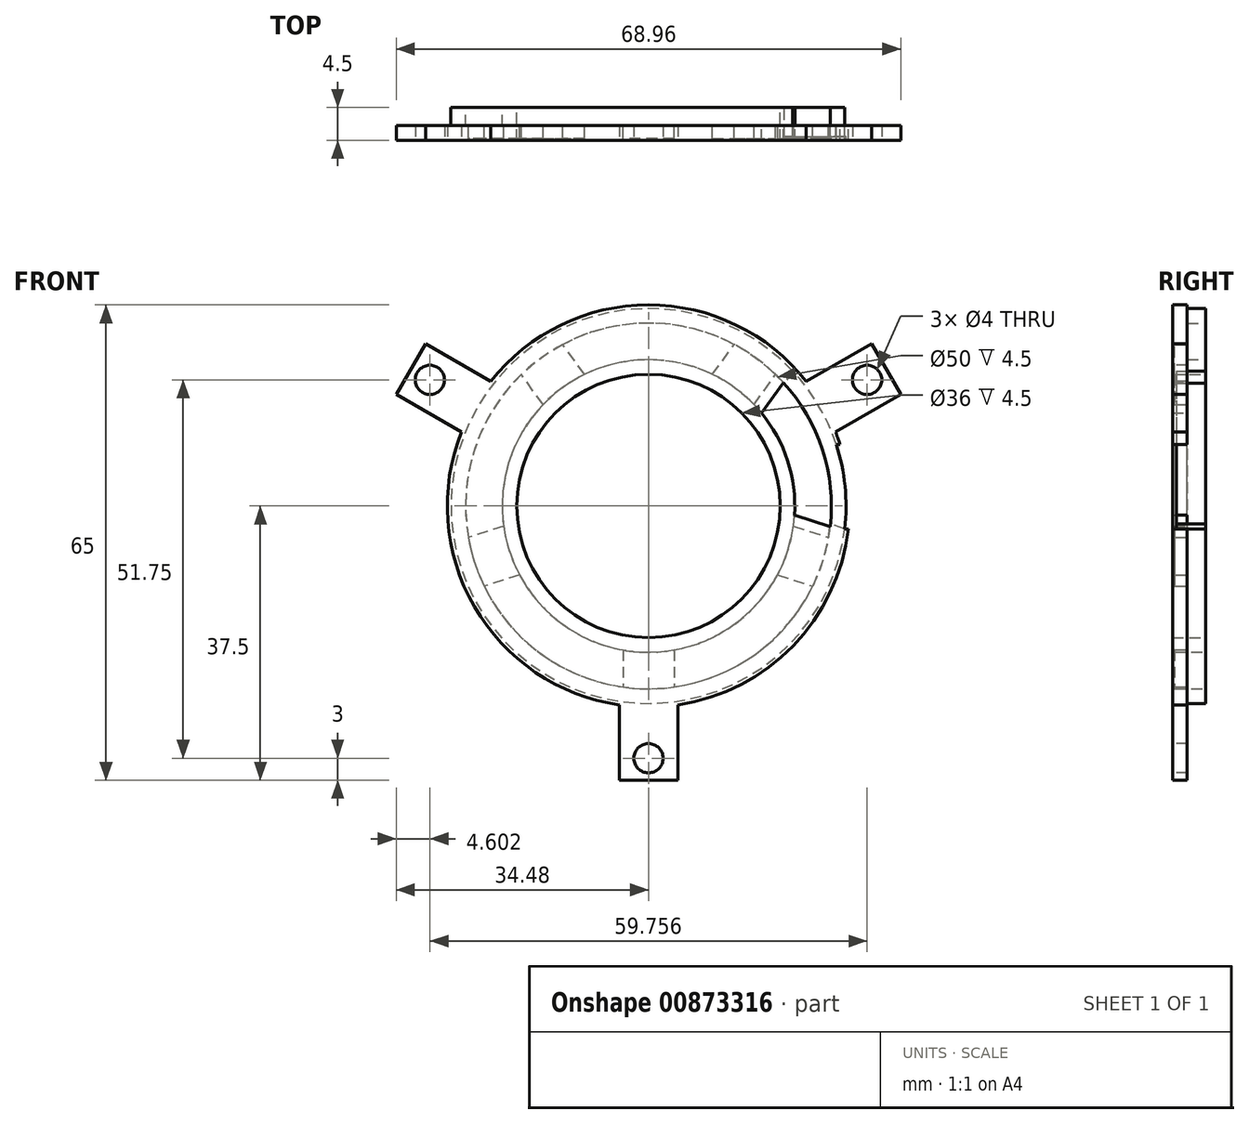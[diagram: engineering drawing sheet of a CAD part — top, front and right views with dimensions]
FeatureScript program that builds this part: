
annotation { "Feature Type Name" : "Feature", "Feature Type Description" : "" }
export const myFeature = defineFeature(function(context is Context, id is Id, definition is map)
    precondition{}
    {
        {
            var Q0;
            Q0=qCreatedBy(makeId("Right.planeOp"),FACE);
            var sketch = newSketch(context, id + "F0", { "sketchPlane" : qUnion([Q0])});
            skLineSegment(sketch, "E0", {"start": v(0, 0) * mm, "end": v(0, 18) * mm});
            skLineSegment(sketch, "E1", {"start": v(0, 18) * mm, "end": v(0, 20) * mm});
            skLineSegment(sketch, "E2", {"start": v(0, 20) * mm, "end": v(0, 25) * mm});
            skLineSegment(sketch, "E3", {"start": v(0, 25) * mm, "end": v(0, 27) * mm});
            skLineSegment(sketch, "E4", {"start": v(0, 27) * mm, "end": v(4.5, 27) * mm});
            skPoint(sketch, "E5.endSnap0", {"position": v(2.25, 27) * mm});
            skLineSegment(sketch, "E6", {"start": v(0, 22.5) * mm, "end": v(2, 22.5) * mm});
            skLineSegment(sketch, "E7", {"start": v(2, 27) * mm, "end": v(2, 0) * mm});
            skLineSegment(sketch, "E8", {"start": v(2, 0) * mm, "end": v(0, 0) * mm});
            skLineSegment(sketch, "E9", {"start": v(0, 25) * mm, "end": v(2.25, 25) * mm});
            skLineSegment(sketch, "E10", {"start": v(0, 20) * mm, "end": v(2.25, 20) * mm});
            skLineSegment(sketch, "E11", {"start": v(2, 18) * mm, "end": v(2.25, 18) * mm});
            skLineSegment(sketch, "E12", {"start": v(2, 18) * mm, "end": v(0, 18) * mm});
            skLineSegment(sketch, "E13", {"start": v(2.25, 25) * mm, "end": v(4.5, 25) * mm});
            skLineSegment(sketch, "E14", {"start": v(4.5, 25) * mm, "end": v(4.5, 27) * mm});
            skLineSegment(sketch, "E15", {"start": v(2.25, 20) * mm, "end": v(4.5, 20) * mm});
            skLineSegment(sketch, "E16", {"start": v(4.5, 20) * mm, "end": v(4.5, 18) * mm});
            skLineSegment(sketch, "E17", {"start": v(4.5, 18) * mm, "end": v(2.25, 18) * mm});
            skSolve(sketch);
        }
        {
            var Q0;
            Q0 = qSketchRegion(id + "F0", true);
            var Q1;
            Q1=sQuery(id+"F0.wireOp",EDGE,"E8");
            revolve(context, id + "F1", {"surfaceOperationType" : NewSurfaceOperationType.NEW, "entities" : qUnion([Q0]), "axis" : qUnion([Q1]), "revolveType" : RevolveType.FULL});
        }
        {
            var Q0;
            {var subQ0=sQuery(id+"F0.wireOp",EDGE,"E7");var subQ1=makeQuery(id+"F0.imprint","INTERSECT",VERTEX,{"derivedFrom":[sQuery(id+"F0.wireOp",EDGE,"E6"),subQ0]});Q0=makeQuery(id+"F1.opRevolve","SWEPT_FACE",FACE,{"disambiguationData":[OSD([subQ0]),TDD([makeQuery(id+"F0.imprint","IMPRINT",EDGE,{"disambiguationData":[TD([[subQ1,1.0]])],"derivedFrom":subQ0}),makeQuery(id+"F0.imprint","IMPRINT",EDGE,{"disambiguationData":[TD([[subQ1,-1.0]])],"derivedFrom":subQ0})])]});}
            var sketch = newSketch(context, id + "F2", { "sketchPlane" : qUnion([Q0])});
            skCircle(sketch, "E18", {"center": v(0, 0) * mm, "radius": 25 * mm});
            skCircle(sketch, "E19", {"center": v(0, 0) * mm, "radius": 20 * mm});
            skLineSegment(sketch, "E20", {"start": v(0, -20) * mm, "end": v(0, -25) * mm});
            skLineSegment(sketch, "E21", {"start": v(0, -22.5) * mm, "end": v(3.5, -22.5) * mm});
            skLineSegment(sketch, "E22", {"start": v(3.5, -19.7) * mm, "end": v(3.5, -24.75) * mm});
            skLineSegment(sketch, "E23.MirrorCS", {"start": v(-3.5, -19.7) * mm, "end": v(-3.5, -24.75) * mm});
            skLineSegment(sketch, "E24.1.0", {"start": v(19.8, -2.76) * mm, "end": v(24.62, -4.32) * mm});
            skLineSegment(sketch, "E24.1.1", {"start": v(17.65, -9.41) * mm, "end": v(22.46, -10.98) * mm});
            skLineSegment(sketch, "E24.2.0", {"start": v(8.74, 17.99) * mm, "end": v(11.72, 22.08) * mm});
            skLineSegment(sketch, "E24.2.1", {"start": v(14.4, 13.87) * mm, "end": v(17.38, 17.97) * mm});
            skLineSegment(sketch, "E24.3.0", {"start": v(-14.4, 13.87) * mm, "end": v(-17.38, 17.97) * mm});
            skLineSegment(sketch, "E24.3.1", {"start": v(-8.74, 17.99) * mm, "end": v(-11.72, 22.08) * mm});
            skLineSegment(sketch, "E24.4.0", {"start": v(-17.65, -9.41) * mm, "end": v(-22.46, -10.98) * mm});
            skLineSegment(sketch, "E24.4.1", {"start": v(-19.8, -2.76) * mm, "end": v(-24.62, -4.32) * mm});
            skLineSegment(sketch, "E25", {"start": v(-22.22, -3.54) * mm, "end": v(-22.68, -2.11) * mm});
            skLineSegment(sketch, "E26", {"start": v(-15.9, 15.92) * mm, "end": v(-17.1, 15.04) * mm});
            skCircle(sketch, "E27", {"center": v(0, 0) * mm, "radius": 27 * mm});
            skLineSegment(sketch, "E28", {"start": v(-22.68, -2.11) * mm, "end": v(-26.78, -3.44) * mm});
            skLineSegment(sketch, "E29", {"start": v(-26.78, -3.44) * mm, "end": v(-19.96, -1.23) * mm});
            skLineSegment(sketch, "E30", {"start": v(-17.1, 15.04) * mm, "end": v(-19.64, 18.53) * mm});
            skLineSegment(sketch, "E31", {"start": v(-19.64, 18.53) * mm, "end": v(-15.43, 12.73) * mm});
            skSolve(sketch);
        }
        {
            var Q0;
            {var subQ0=sQuery(id+"F2.wireOp",EDGE,"E24.4.0");Q0=makeQuery(id+"F2.imprint","IMPRINT",FACE,{"disambiguationData":[TD([[makeQuery(id+"F2.imprint","IMPRINT",EDGE,{"derivedFrom":subQ0}),-1.0]])]});}
            var Q1;
            {var subQ0=sQuery(id+"F2.wireOp",EDGE,"E24.3.0");Q1=makeQuery(id+"F2.imprint","IMPRINT",FACE,{"disambiguationData":[TD([[makeQuery(id+"F2.imprint","IMPRINT",EDGE,{"derivedFrom":subQ0}),-1.0]])]});}
            var Q2;
            {var subQ0=sQuery(id+"F2.wireOp",EDGE,"E24.2.0");Q2=makeQuery(id+"F2.imprint","IMPRINT",FACE,{"disambiguationData":[TD([[makeQuery(id+"F2.imprint","IMPRINT",EDGE,{"derivedFrom":subQ0}),-1.0]])]});}
            var Q3;
            {var subQ6=sQuery(id+"F2.wireOp",EDGE,"E23.MirrorCS");Q3=makeQuery(id+"F2.imprint","IMPRINT",FACE,{"disambiguationData":[TD([[makeQuery(id+"F2.imprint","IMPRINT",EDGE,{"derivedFrom":subQ6}),1.0]])]});}
            var Q4;
            {var subQ5=sQuery(id+"F2.wireOp",EDGE,"E21");Q4=makeQuery(id+"F2.imprint","IMPRINT",FACE,{"disambiguationData":[TD([[makeQuery(id+"F2.imprint","IMPRINT",EDGE,{"derivedFrom":subQ5}),1.0]])]});}
            var Q5;
            {var subQ5=sQuery(id+"F2.wireOp",EDGE,"E21");Q5=makeQuery(id+"F2.imprint","IMPRINT",FACE,{"disambiguationData":[TD([[makeQuery(id+"F2.imprint","IMPRINT",EDGE,{"derivedFrom":subQ5}),-1.0]])]});}
            var Q6;
            {var subQ0=sQuery(id+"F2.wireOp",EDGE,"E24.1.0");Q6=makeQuery(id+"F2.imprint","IMPRINT",FACE,{"disambiguationData":[TD([[makeQuery(id+"F2.imprint","IMPRINT",EDGE,{"derivedFrom":subQ0}),-1.0]])]});}
            extrude(context, id + "F3", {"entities" : qUnion([Q0, Q1, Q2, Q3, Q4, Q5, Q6]), "operationType" : NewBodyOperationType.REMOVE, "oppositeDirection" : true, "depth" : .6 * mm, "offsetDistance" : 25 * mm});
        }
        {
            var Q0;
            {var subQ0=sQuery(id+"F2.wireOp",EDGE,"E24.2.0");Q0=makeQuery(id+"F2.imprint","IMPRINT",FACE,{"disambiguationData":[TD([[makeQuery(id+"F2.imprint","IMPRINT",EDGE,{"derivedFrom":subQ0}),-1.0]])]});}
            var Q1;
            {var subQ0=sQuery(id+"F2.wireOp",EDGE,"E24.3.1");Q1=makeQuery(id+"F2.imprint","IMPRINT",FACE,{"disambiguationData":[TD([[makeQuery(id+"F2.imprint","IMPRINT",EDGE,{"derivedFrom":subQ0}),1.0]])]});}
            var Q2;
            {var subQ0=sQuery(id+"F2.wireOp",EDGE,"E24.1.0");Q2=makeQuery(id+"F2.imprint","IMPRINT",FACE,{"disambiguationData":[TD([[makeQuery(id+"F2.imprint","IMPRINT",EDGE,{"derivedFrom":subQ0}),-1.0]])]});}
            var Q3;
            {var subQ3=sQuery(id+"F2.wireOp",EDGE,"E23.MirrorCS");Q3=makeQuery(id+"F2.imprint","IMPRINT",FACE,{"disambiguationData":[TD([[makeQuery(id+"F2.imprint","IMPRINT",EDGE,{"derivedFrom":subQ3}),1.0]])]});}
            var Q4;
            {var subQ3=sQuery(id+"F2.wireOp",EDGE,"E21");Q4=makeQuery(id+"F2.imprint","IMPRINT",FACE,{"disambiguationData":[TD([[makeQuery(id+"F2.imprint","IMPRINT",EDGE,{"derivedFrom":subQ3}),1.0]])]});}
            var Q5;
            {var subQ3=sQuery(id+"F2.wireOp",EDGE,"E21");Q5=makeQuery(id+"F2.imprint","IMPRINT",FACE,{"disambiguationData":[TD([[makeQuery(id+"F2.imprint","IMPRINT",EDGE,{"derivedFrom":subQ3}),-1.0]])]});}
            var Q6;
            {var subQ1=sQuery(id+"F2.wireOp",EDGE,"E24.4.0");Q6=makeQuery(id+"F2.imprint","IMPRINT",FACE,{"disambiguationData":[TD([[makeQuery(id+"F2.imprint","IMPRINT",EDGE,{"derivedFrom":subQ1}),-1.0]])]});}
            extrude(context, id + "F4", {"entities" : qUnion([Q0, Q1, Q2, Q3, Q4, Q5, Q6]), "operationType" : NewBodyOperationType.REMOVE, "oppositeDirection" : true, "depth" : 1.75 * mm, "offsetDistance" : 25 * mm});
        }
        {
            var Q0;
            Q0=makeQuery(id+"F1.opRevolve","SWEPT_FACE",FACE,{"disambiguationData":[OSD([sQuery(id+"F0.wireOp",EDGE,"E14")])]});
            var sketch = newSketch(context, id + "F5", { "sketchPlane" : qUnion([Q0])});
            skCircle(sketch, "E32", {"center": v(0, 0) * mm, "radius": 27 * mm});
            skCircle(sketch, "E33", {"center": v(0, 0) * mm, "radius": 25 * mm});
            skLineSegment(sketch, "E34", {"start": v(-26.82, -3.14) * mm, "end": v(-24.88, -2.45) * mm});
            skLineSegment(sketch, "E35", {"start": v(-19.72, 18.44) * mm, "end": v(-18.55, 16.76) * mm});
            skSolve(sketch);
        }
        {
            var Q0;
            {var subQ0=sQuery(id+"F5.wireOp",EDGE,"E34");Q0=makeQuery(id+"F5.imprint","IMPRINT",FACE,{"disambiguationData":[TD([[makeQuery(id+"F5.imprint","IMPRINT",EDGE,{"derivedFrom":subQ0}),1.0]])]});}
            extrude(context, id + "F6", {"entities" : qUnion([Q0]), "operationType" : NewBodyOperationType.REMOVE, "oppositeDirection" : true, "depth" : 4 * mm, "offsetDistance" : 25 * mm});
        }
        {
            var Q0;
            {var subQ6=sQuery(id+"F2.wireOp",EDGE,"E29");var subQ7=makeQuery(id+"F2.imprint","INTERSECT",VERTEX,{"derivedFrom":[sQuery(id+"F2.wireOp",EDGE,"E25"),subQ6]});Q0=makeQuery(id+"F2.imprint","IMPRINT",FACE,{"disambiguationData":[TD([[makeQuery(id+"F2.imprint","IMPRINT",EDGE,{"disambiguationData":[TD([[subQ7,1.0]])],"derivedFrom":subQ6}),1.0]])]});}
            var sketch = newSketch(context, id + "F7", { "sketchPlane" : qUnion([Q0])});
            skCircle(sketch, "E36", {"center": v(0, 0) * mm, "radius": 18 * mm});
            skSolve(sketch);
        }
        {
            var Q0;
            Q0 = qSketchRegion(id + "F7", true);
            extrude(context, id + "F8", {"entities" : qUnion([Q0]), "operationType" : NewBodyOperationType.REMOVE, "oppositeDirection" : true, "depth" : 2 * mm, "offsetDistance" : 25 * mm});
        }
        {
            var Q0;
            Q0=makeQuery(id+"F1.opRevolve","SWEPT_FACE",FACE,{"disambiguationData":[OSD([sQuery(id+"F0.wireOp",EDGE,"E0"),sQuery(id+"F0.wireOp",EDGE,"E1"),sQuery(id+"F0.wireOp",EDGE,"E2"),sQuery(id+"F0.wireOp",EDGE,"E3")])]});
            var sketch = newSketch(context, id + "F9", { "sketchPlane" : qUnion([Q0])});
            skCircle(sketch, "E37", {"center": v(0, 0) * mm, "radius": 27.5 * mm});
            skLineSegment(sketch, "E38", {"start": v(0, -27.5) * mm, "end": v(0, -37.5) * mm});
            skLineSegment(sketch, "E39", {"start": v(0, -37.5) * mm, "end": v(-4, -37.5) * mm});
            skLineSegment(sketch, "E40", {"start": v(-4, -37.5) * mm, "end": v(-4, -27.2) * mm});
            skLineSegment(sketch, "E41.MirrorCS", {"start": v(0, -37.5) * mm, "end": v(4, -37.5) * mm});
            skLineSegment(sketch, "E42.MirrorCS", {"start": v(4, -37.5) * mm, "end": v(4, -27.2) * mm});
            skLineSegment(sketch, "E43.bottom", {"start": v(0, -37.5) * mm, "end": v(0, -37.5) * mm});
            skLineSegment(sketch, "E43.top", {"start": v(0, -34.5) * mm, "end": v(0, -34.5) * mm});
            skLineSegment(sketch, "E43.left", {"start": v(0, -37.5) * mm, "end": v(0, -34.5) * mm});
            skLineSegment(sketch, "E43.right", {"start": v(0, -37.5) * mm, "end": v(0, -34.5) * mm});
            skCircle(sketch, "E44", {"center": v(0, -34.5) * mm, "radius": 2 * mm});
            skLineSegment(sketch, "E45.1.0", {"start": v(34.48, 15.29) * mm, "end": v(25.56, 10.14) * mm});
            skLineSegment(sketch, "E45.1.1", {"start": v(30.48, 22.21) * mm, "end": v(21.56, 17.07) * mm});
            skLineSegment(sketch, "E45.1.2", {"start": v(32.48, 18.75) * mm, "end": v(30.48, 22.21) * mm});
            skLineSegment(sketch, "E45.1.3", {"start": v(32.48, 18.75) * mm, "end": v(34.48, 15.29) * mm});
            skCircle(sketch, "E45.1.4", {"center": v(29.88, 17.25) * mm, "radius": 2 * mm});
            skLineSegment(sketch, "E45.2.0", {"start": v(-30.48, 22.21) * mm, "end": v(-21.56, 17.07) * mm});
            skLineSegment(sketch, "E45.2.1", {"start": v(-34.48, 15.29) * mm, "end": v(-25.56, 10.14) * mm});
            skLineSegment(sketch, "E45.2.2", {"start": v(-32.48, 18.75) * mm, "end": v(-34.48, 15.29) * mm});
            skLineSegment(sketch, "E45.2.3", {"start": v(-32.48, 18.75) * mm, "end": v(-30.48, 22.21) * mm});
            skCircle(sketch, "E45.2.4", {"center": v(-29.88, 17.25) * mm, "radius": 2 * mm});
            skLineSegment(sketch, "E46", {"start": v(0, 0) * mm, "end": v(-19.54, -19.35) * mm});
            skSolve(sketch);
        }
        {
            var Q0;
            {var subQ0=sQuery(id+"F9.wireOp",EDGE,"E41.MirrorCS");Q0=makeQuery(id+"F9.imprint","IMPRINT",FACE,{"disambiguationData":[TD([[makeQuery(id+"F9.imprint","IMPRINT",EDGE,{"derivedFrom":subQ0}),1.0]])]});}
            var Q1;
            {var subQ6=sQuery(id+"F9.wireOp",EDGE,"E39");Q1=makeQuery(id+"F9.imprint","IMPRINT",FACE,{"disambiguationData":[TD([[makeQuery(id+"F9.imprint","IMPRINT",EDGE,{"derivedFrom":subQ6}),-1.0]])]});}
            var Q2;
            Q2=makeQuery(id+"F9.imprint","IMPRINT",FACE,{"disambiguationData":[TD([[makeQuery(id+"F9.imprint","IMPRINT",EDGE,{"derivedFrom":makeQuery(id+"F1.opRevolve","SWEPT_EDGE",EDGE,{"disambiguationData":[OSD([sQuery(id+"F0.wireOp",EDGE,"E3"),sQuery(id+"F0.wireOp",EDGE,"E4")])]})}),1.0]])]});
            var Q3;
            {var subQ1=sQuery(id+"F9.wireOp",EDGE,"E45.1.0");Q3=makeQuery(id+"F9.imprint","IMPRINT",FACE,{"disambiguationData":[TD([[makeQuery(id+"F9.imprint","IMPRINT",EDGE,{"derivedFrom":subQ1}),-1.0]])]});}
            var Q4;
            {var subQ0=sQuery(id+"F9.wireOp",EDGE,"E45.2.0");Q4=makeQuery(id+"F9.imprint","IMPRINT",FACE,{"disambiguationData":[TD([[makeQuery(id+"F9.imprint","IMPRINT",EDGE,{"derivedFrom":subQ0}),-1.0]])]});}
            extrude(context, id + "F10", {"entities" : qUnion([Q0, Q1, Q2, Q3, Q4]), "operationType" : NewBodyOperationType.ADD, "depth" : -2 * mm, "offsetDistance" : 25 * mm});
        }
        {
            var Q0;
            {var subQ6=sQuery(id+"F2.wireOp",EDGE,"E29");var subQ7=makeQuery(id+"F2.imprint","INTERSECT",VERTEX,{"derivedFrom":[sQuery(id+"F2.wireOp",EDGE,"E25"),subQ6]});Q0=makeQuery(id+"F2.imprint","IMPRINT",FACE,{"disambiguationData":[TD([[makeQuery(id+"F2.imprint","IMPRINT",EDGE,{"disambiguationData":[TD([[subQ7,1.0]])],"derivedFrom":subQ6}),1.0]])]});}
            extrude(context, id + "F11", {"entities" : qUnion([Q0]), "operationType" : NewBodyOperationType.REMOVE, "oppositeDirection" : true, "depth" : 3 * mm, "offsetDistance" : 25 * mm});
        }
        {
            var Q0;
            Q0=makeQuery(id+"F10.opExtrude","CAP_FACE",FACE,{"disambiguationData":[OSD([sQuery(id+"F0.wireOp",EDGE,"E3"),sQuery(id+"F0.wireOp",EDGE,"E4"),sQuery(id+"F9.wireOp",EDGE,"E37"),sQuery(id+"F9.wireOp",EDGE,"E39"),sQuery(id+"F9.wireOp",EDGE,"E40"),sQuery(id+"F9.wireOp",EDGE,"E41.MirrorCS"),sQuery(id+"F9.wireOp",EDGE,"E42.MirrorCS"),sQuery(id+"F9.wireOp",EDGE,"E44"),sQuery(id+"F9.wireOp",EDGE,"E45.1.0"),sQuery(id+"F9.wireOp",EDGE,"E45.1.1"),sQuery(id+"F9.wireOp",EDGE,"E45.1.2"),sQuery(id+"F9.wireOp",EDGE,"E45.1.3"),sQuery(id+"F9.wireOp",EDGE,"E45.1.4"),sQuery(id+"F9.wireOp",EDGE,"E45.2.0"),sQuery(id+"F9.wireOp",EDGE,"E45.2.1"),sQuery(id+"F9.wireOp",EDGE,"E45.2.2"),sQuery(id+"F9.wireOp",EDGE,"E45.2.3"),sQuery(id+"F9.wireOp",EDGE,"E45.2.4")])],"isStart":false});
            var sketch = newSketch(context, id + "F12", { "sketchPlane" : qUnion([Q0])});
            skLineSegment(sketch, "E47", {"start": v(-26.82, -3.14) * mm, "end": v(-27.32, -3.14) * mm});
            skLineSegment(sketch, "E48", {"start": v(-25.65, 8.43) * mm, "end": v(-26.18, 8.43) * mm});
            skSolve(sketch);
        }
        {
            var Q0;
            {var subQ0=sQuery(id+"F12.wireOp",EDGE,"E47");Q0=makeQuery(id+"F12.imprint","IMPRINT",FACE,{"disambiguationData":[TD([[makeQuery(id+"F12.imprint","IMPRINT",EDGE,{"derivedFrom":subQ0}),-1.0]])]});}
            extrude(context, id + "F13", {"entities" : qUnion([Q0]), "operationType" : NewBodyOperationType.REMOVE, "oppositeDirection" : true, "depth" : 2 * mm, "offsetDistance" : 25 * mm});
        }
    });
